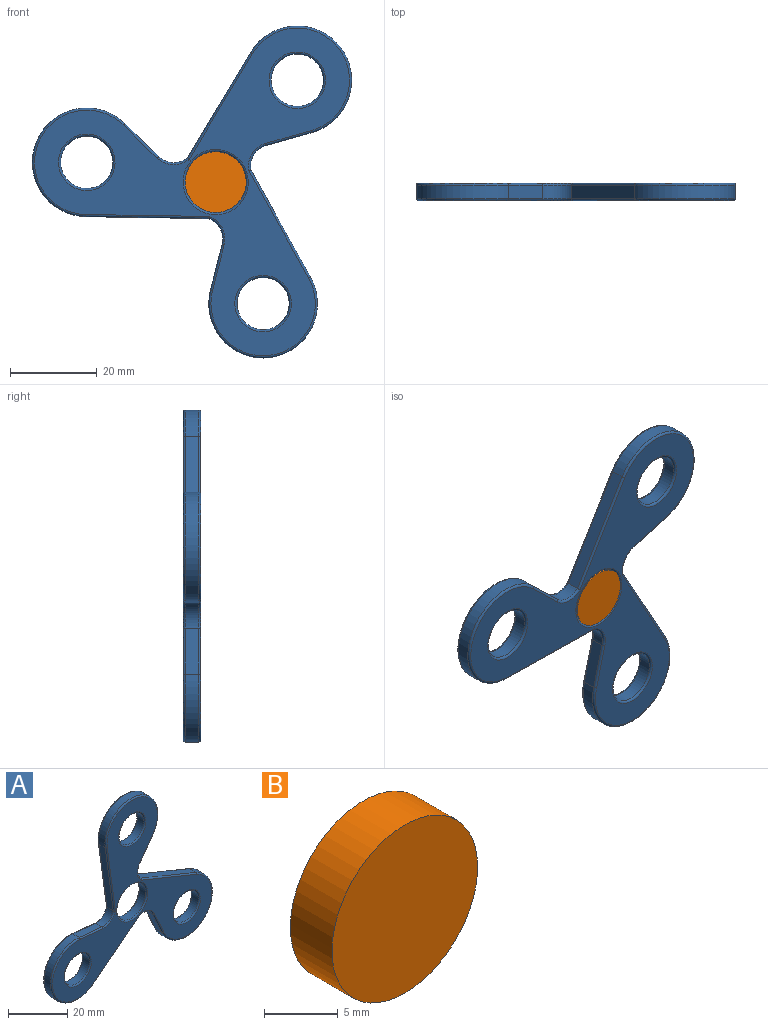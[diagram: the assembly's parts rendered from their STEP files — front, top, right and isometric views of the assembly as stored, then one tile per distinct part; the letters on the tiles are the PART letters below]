
ASSEMBLY  parts=2 mates=1
PART A: 50 faces, bbox 78.1x4x71.6 mm
  f0: plane 27.99x3.84mm, normal (-0.99,0,-0.14), area 84.8mm2, adj f6,f9,f12,f20
  f1: cylinder r=5mm len=6.61mm, axis (0,-1,0), area 21.8mm2, adj f5,f11,f15,f21
  f2: cylinder r=7mm len=14mm, axis (0,-1,0), area 131.9mm2, adj f18,f19
  f3: plane 75.96x69mm, normal (0,1,0), area 1523.2mm2, adj f8,f9,f10,f11,f16,f19,f26,f27
  f4: plane 75.96x69mm, normal (0,-1,0), area 1523.2mm2, adj f12,f13,f14,f15,f17,f18,f30,f31
  f5: plane 8.88x6.34mm, normal (0.81,0,-0.58), area 32.7mm2, adj f1,f6,f10,f14
  f6: cylinder r=12.5mm len=25mm, axis (0,-1,0), area 146.2mm2, adj f0,f5,f8,f13
  f7: cylinder r=6mm len=12mm, axis (0,-1,0), area 113.1mm2, adj f16,f17
  f8: torus R=12mm, axis (0,-1,0), area 37.7mm2, adj f3,f6,f9,f10
  f9: cylinder r=0.5mm len=28.14mm, axis (-0.14,0,0.99), area 22.2mm2, adj f0,f3,f8,f29
  f10: cylinder r=0.5mm len=9.17mm, axis (-0.58,0,-0.81), area 8.6mm2, adj f3,f5,f8,f11
  f11: torus R=5.5mm, axis (0,-1,0), area 6mm2, adj f1,f3,f10,f41
  f12: cylinder r=0.5mm len=28.14mm, axis (0.14,0,-0.99), area 22.2mm2, adj f0,f4,f13,f33
  f13: torus R=12mm, axis (0,-1,0), area 37.7mm2, adj f4,f6,f12,f14
  f14: cylinder r=0.5mm len=9.17mm, axis (0.58,0,0.81), area 8.6mm2, adj f4,f5,f13,f15
  f15: torus R=5.5mm, axis (0,-1,0), area 6mm2, adj f1,f4,f14,f44
  f16: torus R=6.5mm, axis (0,-1,0), area 30.5mm2, adj f3,f7
  f17: torus R=6.5mm, axis (0,-1,0), area 30.5mm2, adj f4,f7
  f18: torus R=7.5mm, axis (0,-1,0), area 35.4mm2, adj f2,f4
  f19: torus R=7.5mm, axis (0,-1,0), area 35.4mm2, adj f2,f3
  f20: cylinder r=5mm len=5.37mm, axis (0,-1,0), area 21.8mm2, adj f0,f23,f29,f33
  f21: plane 26.16x10.67mm, normal (0.38,0,0.93), area 84.8mm2, adj f1,f38,f41,f44
  f22: plane 22.32x17.32mm, normal (0.61,0,-0.79), area 84.8mm2, adj f24,f27,f30,f36
  f23: plane 10.86x3mm, normal (0.1,0,1), area 32.7mm2, adj f20,f24,f28,f32
  f24: cylinder r=12.5mm len=25mm, axis (0,-1,0), area 146.2mm2, adj f22,f23,f26,f31
  f25: cylinder r=6mm len=12mm, axis (0,-1,0), area 113.1mm2, adj f34,f35
  f26: torus R=12mm, axis (0,-1,0), area 37.7mm2, adj f3,f24,f27,f28
  f27: cylinder r=0.5mm len=22.69mm, axis (-0.79,0,-0.61), area 22.2mm2, adj f3,f22,f26,f43
  f28: cylinder r=0.5mm len=10.91mm, axis (1,0,-0.1), area 8.6mm2, adj f3,f23,f26,f29
  f29: torus R=5.5mm, axis (0,-1,0), area 6mm2, adj f3,f9,f20,f28
  f30: cylinder r=0.5mm len=22.69mm, axis (0.79,0,0.61), area 22.2mm2, adj f4,f22,f31,f47
  f31: torus R=12mm, axis (0,-1,0), area 37.7mm2, adj f4,f24,f30,f32
  f32: cylinder r=0.5mm len=10.91mm, axis (-1,0,0.1), area 8.6mm2, adj f4,f23,f31,f33
  f33: torus R=5.5mm, axis (0,-1,0), area 6mm2, adj f4,f12,f20,f32
  f34: torus R=6.5mm, axis (0,-1,0), area 30.5mm2, adj f3,f25
  f35: torus R=6.5mm, axis (0,-1,0), area 30.5mm2, adj f4,f25
  f36: cylinder r=5mm len=6.09mm, axis (0,-1,0), area 21.8mm2, adj f22,f37,f43,f47
  f37: plane 9.93x4.52mm, normal (-0.91,0,-0.41), area 32.7mm2, adj f36,f38,f42,f46
  f38: cylinder r=12.5mm len=24.07mm, axis (0,-1,0), area 146.2mm2, adj f21,f37,f40,f45
  f39: cylinder r=6mm len=12mm, axis (0,-1,0), area 113.1mm2, adj f48,f49
  f40: torus R=12mm, axis (0,-1,0), area 37.7mm2, adj f3,f38,f41,f42
  f41: cylinder r=0.5mm len=26.43mm, axis (0.93,0,-0.38), area 22.2mm2, adj f3,f11,f21,f40
  f42: cylinder r=0.5mm len=10.14mm, axis (-0.41,0,0.91), area 8.6mm2, adj f3,f37,f40,f43
  f43: torus R=5.5mm, axis (0,-1,0), area 6mm2, adj f3,f27,f36,f42
  f44: cylinder r=0.5mm len=26.43mm, axis (-0.93,0,0.38), area 22.2mm2, adj f4,f15,f21,f45
  f45: torus R=12mm, axis (0,-1,0), area 37.7mm2, adj f4,f38,f44,f46
  f46: cylinder r=0.5mm len=10.14mm, axis (0.41,0,-0.91), area 8.6mm2, adj f4,f37,f45,f47
  f47: torus R=5.5mm, axis (0,-1,0), area 6mm2, adj f4,f30,f36,f46
  f48: torus R=6.5mm, axis (0,-1,0), area 30.5mm2, adj f3,f39
  f49: torus R=6.5mm, axis (0,-1,0), area 30.5mm2, adj f4,f39
PART B: 3 faces, bbox 14x4x14 mm
  f0: cylinder r=7mm len=14mm, axis (0,1,0), area 175.9mm2, adj f1,f2
  f1: plane 14x14mm, normal (0,-1,0), area 153.9mm2, adj f0
  f2: plane 14x14mm, normal (0,1,0), area 153.9mm2, adj f0
PLACE A rot(axis=(0,1,0),38.7deg) t=(-26.19,-3.11,7.52)mm
PLACE B t=(-26.19,-3.11,7.52)mm fixed
MATE revolute A.f2 <-> B.f0  axis (0,-1,0) through (-26.19,-7.11,7.52)mm
